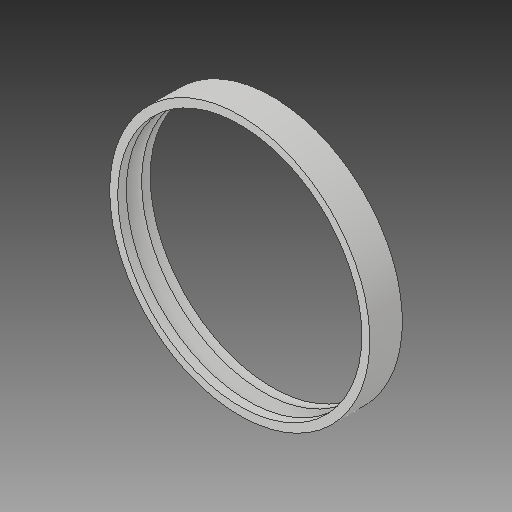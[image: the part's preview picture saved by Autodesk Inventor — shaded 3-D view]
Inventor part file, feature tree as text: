
AUTODESK INVENTOR PART (.ipt)
format: ipt  version: 2018 (Build 220112000, 112)  size: 128,000 bytes
history: native  units: in
note: dims shown in document units (in); Inventor stores cm internally (conversion verified against a paired STEP export)
features: revolve x1, sketch x1
ambient origin geometry x8: Origin, YZ Plane, XZ Plane, XY Plane, X Axis, Y Axis, Z Axis, Center Point
bodies: Solid1 (feature_tree)
feature tree (2):
  revolve  "Revolution1"  [1 undecoded]
  sketch  "Sketch1"  dims[d1=1.875in d2=0.124in d3=0.25in d4=0.25in d5=0.0675in d6=0.135in d7=90.0deg]
note: 1 required parameter value undecoded (feature->parameter linkage not recoverable at this tier; creation-order binding heuristic only, values carry confidence <= 0.55)
